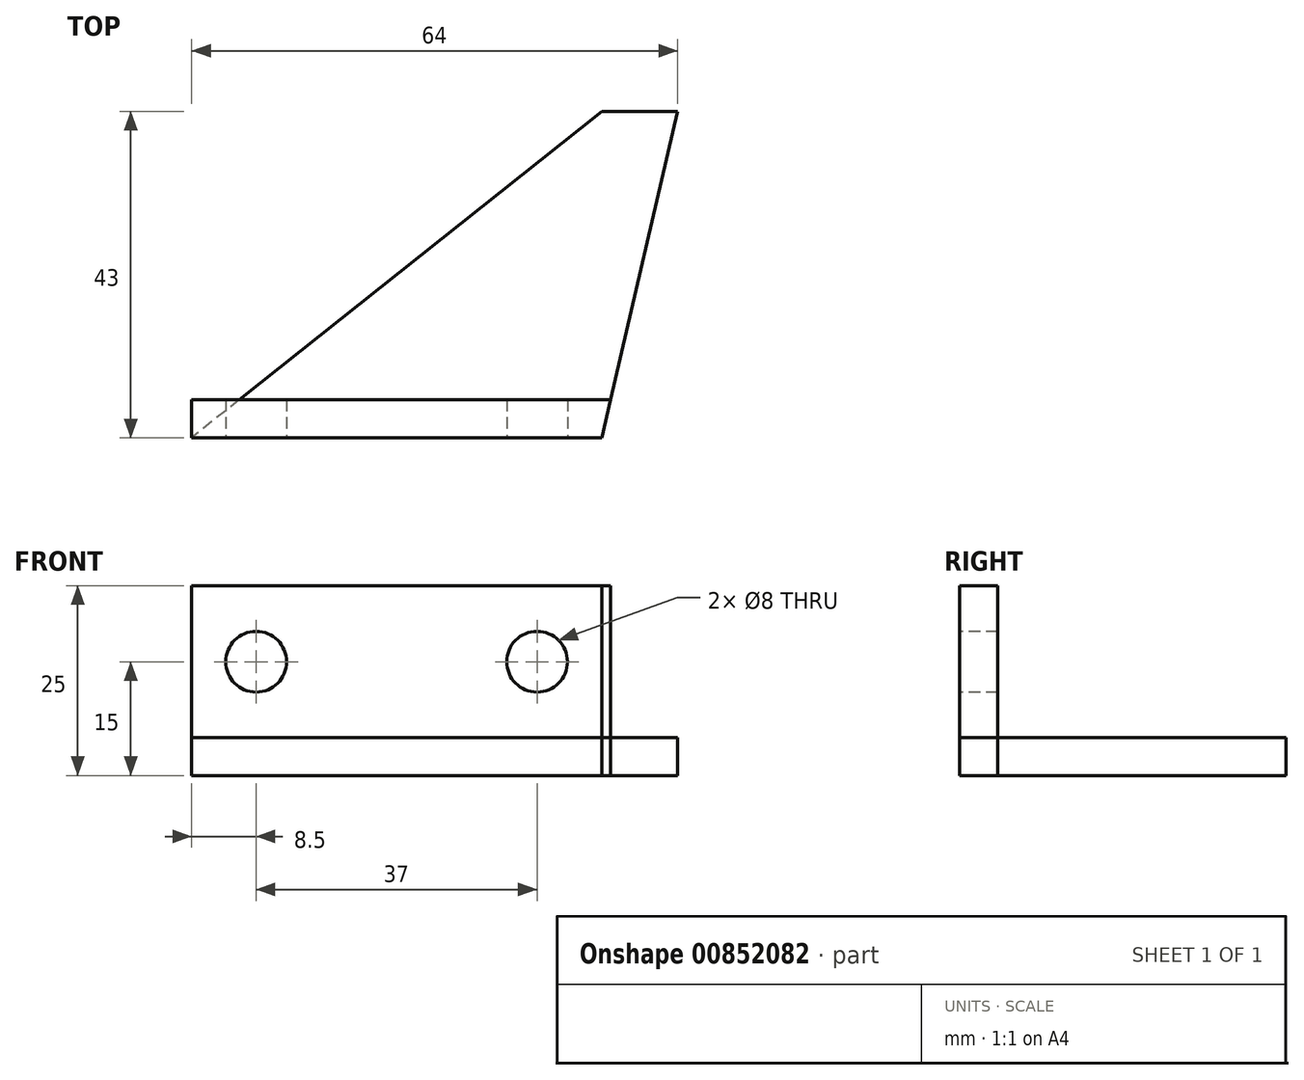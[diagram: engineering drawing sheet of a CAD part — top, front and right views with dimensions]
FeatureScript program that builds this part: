
annotation { "Feature Type Name" : "Feature", "Feature Type Description" : "" }
export const myFeature = defineFeature(function(context is Context, id is Id, definition is map)
    precondition{}
    {
        {
            var Q0;
            Q0=qCreatedBy(makeId("Top.planeOp"),FACE);
            var sketch = newSketch(context, id + "F0", { "sketchPlane" : qUnion([Q0])});
            skLineSegment(sketch, "E0.bottom", {"start": v(27, 21.5) * mm, "end": v(-27, 21.5) * mm});
            skLineSegment(sketch, "E0.top", {"start": v(27, -21.5) * mm, "end": v(-27, -21.5) * mm});
            skLineSegment(sketch, "E0.left", {"start": v(27, 21.5) * mm, "end": v(27, -21.5) * mm});
            skLineSegment(sketch, "E0.right", {"start": v(-27, 21.5) * mm, "end": v(-27, -21.5) * mm});
            skPoint(sketch, "E0.middle", {"position": v(0, 0) * mm});
            skLineSegment(sketch, "E1", {"start": v(27, 21.5) * mm, "end": v(37, 21.5) * mm});
            skLineSegment(sketch, "E2", {"start": v(37, 21.5) * mm, "end": v(27, -21.5) * mm});
            skLineSegment(sketch, "E3", {"start": v(27, 21.5) * mm, "end": v(-27, -21.5) * mm});
            skLineSegment(sketch, "E4", {"start": v(-27, -21.5) * mm, "end": v(-27, -16.5) * mm});
            skLineSegment(sketch, "E5", {"start": v(-27, -16.5) * mm, "end": v(28.16, -16.5) * mm});
            skSolve(sketch);
        }
        {
            var Q0;
            {var subQ0=sQuery(id+"F0.wireOp",EDGE,"E2");var subQ3=sQuery(id+"F0.wireOp",EDGE,"E5");var subQ5=makeQuery(id+"F0.imprint","INTERSECT",VERTEX,{"derivedFrom":[subQ0,subQ3]});Q0=makeQuery(id+"F0.imprint","IMPRINT",FACE,{"disambiguationData":[TD([[makeQuery(id+"F0.imprint","IMPRINT",EDGE,{"disambiguationData":[TD([[subQ5,1.0]])],"derivedFrom":subQ3}),-1.0]])]});}
            var Q1;
            {var subQ0=sQuery(id+"F0.wireOp",EDGE,"E0.top");Q1=makeQuery(id+"F0.imprint","IMPRINT",FACE,{"disambiguationData":[TD([[makeQuery(id+"F0.imprint","IMPRINT",EDGE,{"derivedFrom":subQ0}),-1.0]])]});}
            var Q2;
            {var subQ0=sQuery(id+"F0.wireOp",EDGE,"E3");var subQ3=sQuery(id+"F0.wireOp",EDGE,"E5");var subQ5=makeQuery(id+"F0.imprint","INTERSECT",VERTEX,{"derivedFrom":[subQ0,subQ3]});Q2=makeQuery(id+"F0.imprint","IMPRINT",FACE,{"disambiguationData":[TD([[makeQuery(id+"F0.imprint","IMPRINT",EDGE,{"disambiguationData":[TD([[subQ5,-1.0]])],"derivedFrom":subQ3}),1.0]])]});}
            var Q3;
            {var subQ0=sQuery(id+"F0.wireOp",EDGE,"E1");Q3=makeQuery(id+"F0.imprint","IMPRINT",FACE,{"disambiguationData":[TD([[makeQuery(id+"F0.imprint","IMPRINT",EDGE,{"derivedFrom":subQ0}),-1.0]])]});}
            extrude(context, id + "F1", {"entities" : qUnion([Q0, Q1, Q2, Q3]), "depth" : 5 * mm, "offsetDistance" : 25 * mm});
        }
        {
            var Q0;
            {var subQ0=sQuery(id+"F0.wireOp",EDGE,"E0.top");Q0=makeQuery(id+"F0.imprint","IMPRINT",FACE,{"disambiguationData":[TD([[makeQuery(id+"F0.imprint","IMPRINT",EDGE,{"derivedFrom":subQ0}),-1.0]])]});}
            var Q1;
            {var subQ0=sQuery(id+"F0.wireOp",EDGE,"E2");var subQ3=sQuery(id+"F0.wireOp",EDGE,"E5");var subQ5=makeQuery(id+"F0.imprint","INTERSECT",VERTEX,{"derivedFrom":[subQ0,subQ3]});Q1=makeQuery(id+"F0.imprint","IMPRINT",FACE,{"disambiguationData":[TD([[makeQuery(id+"F0.imprint","IMPRINT",EDGE,{"disambiguationData":[TD([[subQ5,1.0]])],"derivedFrom":subQ3}),-1.0]])]});}
            var Q2;
            {var subQ0=sQuery(id+"F0.wireOp",EDGE,"E3");var subQ3=sQuery(id+"F0.wireOp",EDGE,"E5");var subQ5=makeQuery(id+"F0.imprint","INTERSECT",VERTEX,{"derivedFrom":[subQ0,subQ3]});Q2=makeQuery(id+"F0.imprint","IMPRINT",FACE,{"disambiguationData":[TD([[makeQuery(id+"F0.imprint","IMPRINT",EDGE,{"disambiguationData":[TD([[subQ5,1.0]])],"derivedFrom":subQ3}),-1.0]])]});}
            extrude(context, id + "F2", {"entities" : qUnion([Q0, Q1, Q2]), "depth" : 25 * mm, "offsetDistance" : 25 * mm});
        }
        {
            var Q0;
            Q0=makeQuery(id+"F2.opExtrude","SWEPT_FACE",FACE,{"disambiguationData":[OSD([sQuery(id+"F0.wireOp",EDGE,"E0.top")])]});
            var sketch = newSketch(context, id + "F3", { "sketchPlane" : qUnion([Q0])});
            skLineSegment(sketch, "E6", {"start": v(0, 0) * mm, "end": v(0, 15) * mm});
            skLineSegment(sketch, "E7", {"start": v(0, 15) * mm, "end": v(18.5, 15) * mm});
            skLineSegment(sketch, "E8", {"start": v(0, 15) * mm, "end": v(-18.5, 15) * mm});
            skCircle(sketch, "E9", {"center": v(-18.5, 15) * mm, "radius": 4 * mm});
            skCircle(sketch, "E10", {"center": v(18.5, 15) * mm, "radius": 4 * mm});
            skSolve(sketch);
        }
        {
            var Q0;
            Q0=makeQuery(id+"F3.imprint","IMPRINT",FACE,{"disambiguationData":[TD([[makeQuery(id+"F3.imprint","IMPRINT",EDGE,{"derivedFrom":sQuery(id+"F3.wireOp",EDGE,"E9")}),1.0]])]});
            var Q1;
            Q1=makeQuery(id+"F3.imprint","IMPRINT",FACE,{"disambiguationData":[TD([[makeQuery(id+"F3.imprint","IMPRINT",EDGE,{"derivedFrom":sQuery(id+"F3.wireOp",EDGE,"E10")}),1.0]])]});
            extrude(context, id + "F4", {"entities" : qUnion([Q0, Q1]), "operationType" : NewBodyOperationType.REMOVE, "oppositeDirection" : true, "depth" : 10 * mm, "offsetDistance" : 25 * mm});
        }
    });
